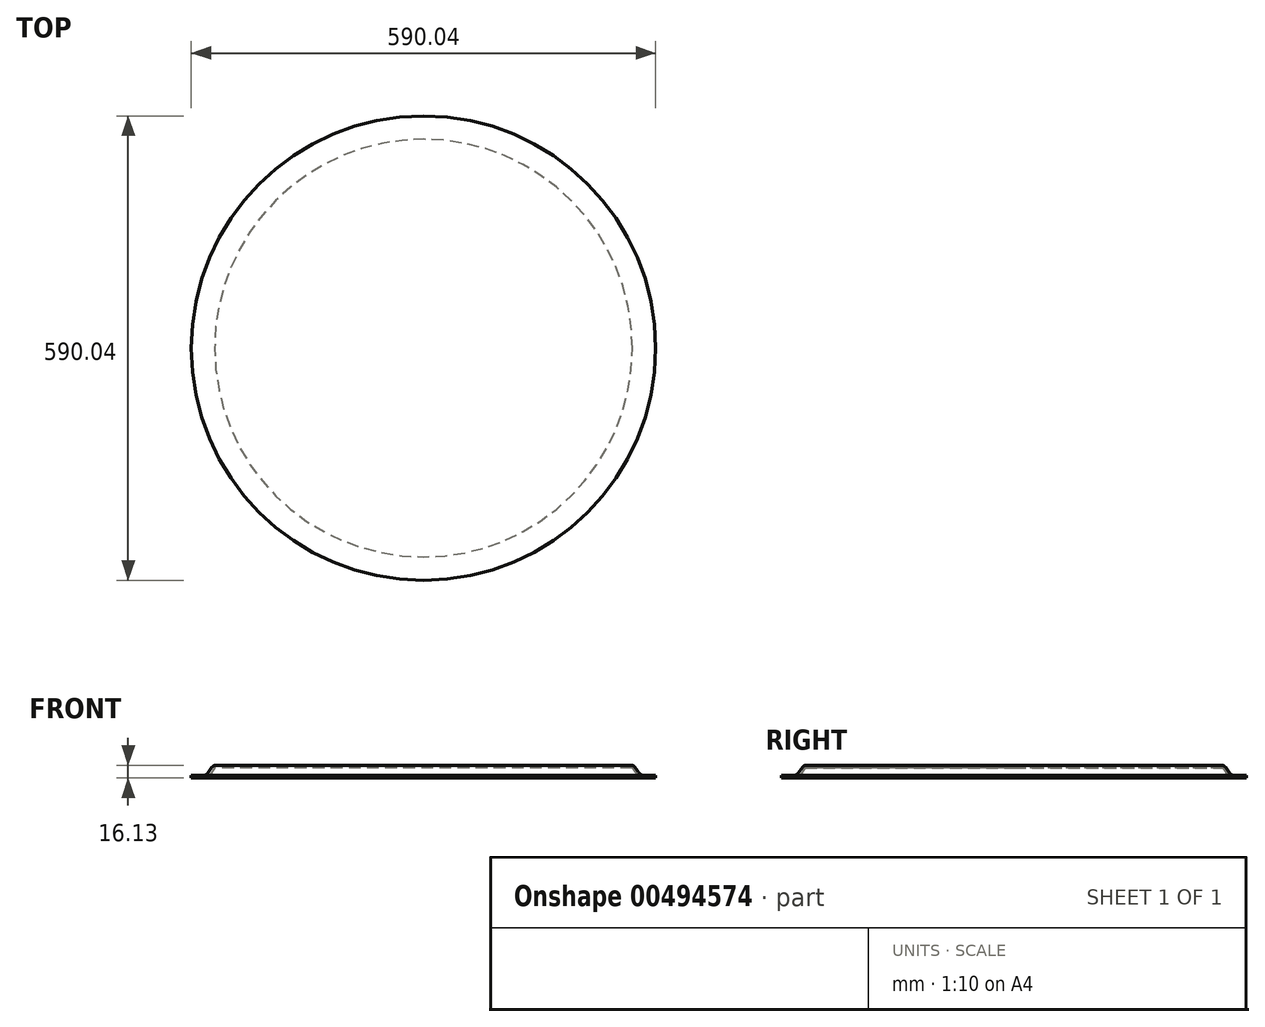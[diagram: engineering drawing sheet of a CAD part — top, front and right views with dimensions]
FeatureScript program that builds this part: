
annotation { "Feature Type Name" : "Feature", "Feature Type Description" : "" }
export const myFeature = defineFeature(function(context is Context, id is Id, definition is map)
    precondition{}
    {
        {
            var Q0;
            Q0=qCreatedBy(makeId("Front.planeOp"),FACE);
            var sketch = newSketch(context, id + "F0", { "sketchPlane" : qUnion([Q0])});
            skLineSegment(sketch, "E0", {"start": v(0, 0) * mm, "end": v(263.75, 0) * mm});
            skLineSegment(sketch, "E1", {"start": v(279.27, -12.7) * mm, "end": v(295.02, -12.7) * mm});
            skLineSegment(sketch, "E2", {"start": v(274.07, -10) * mm, "end": v(268.94, -2.7) * mm});
            skPoint(sketch, "E3.visualSharp", {"position": v(275.97, -12.7) * mm});
            skArc(sketch, "E3.filletArc", {"start": v(274.07, -10) * mm, "mid": v(276.34, -11.98) * mm, "end": v(279.27, -12.7) * mm});
            skPoint(sketch, "E4.visualSharp", {"position": v(267.05, 0) * mm});
            skArc(sketch, "E4.filletArc", {"start": v(268.94, -2.7) * mm, "mid": v(266.68, -0.72) * mm, "end": v(263.75, 0) * mm});
            skLineSegment(sketch, "E5.0", {"start": v(279.27, -16.13) * mm, "end": v(295.02, -16.13) * mm});
            skArc(sketch, "E5.1", {"start": v(271.27, -11.97) * mm, "mid": v(274.76, -15.03) * mm, "end": v(279.27, -16.13) * mm});
            skLineSegment(sketch, "E5.2", {"start": v(271.27, -11.97) * mm, "end": v(265.27, -3.43) * mm});
            skLineSegment(sketch, "E5.3", {"start": v(0, -3.43) * mm, "end": v(265.27, -3.43) * mm});
            skLineSegment(sketch, "E6", {"start": v(295.02, -12.7) * mm, "end": v(295.02, -16.13) * mm});
            skLineSegment(sketch, "E7", {"start": v(0, 0) * mm, "end": v(0, -3.43) * mm});
            skSolve(sketch);
        }
        {
            var Q0;
            Q0=makeQuery(id+"F0.imprint","IMPRINT",FACE,{"disambiguationData":[TD([[makeQuery(id+"F0.imprint","IMPRINT",EDGE,{"derivedFrom":sQuery(id+"F0.wireOp",EDGE,"E0")}),-1.0]])]});
            var Q1;
            Q1=sQuery(id+"F0.wireOp",EDGE,"E7");
            revolve(context, id + "F1", {"entities" : qUnion([Q0]), "axis" : qUnion([Q1]), "revolveType" : RevolveType.FULL});
        }
    });
